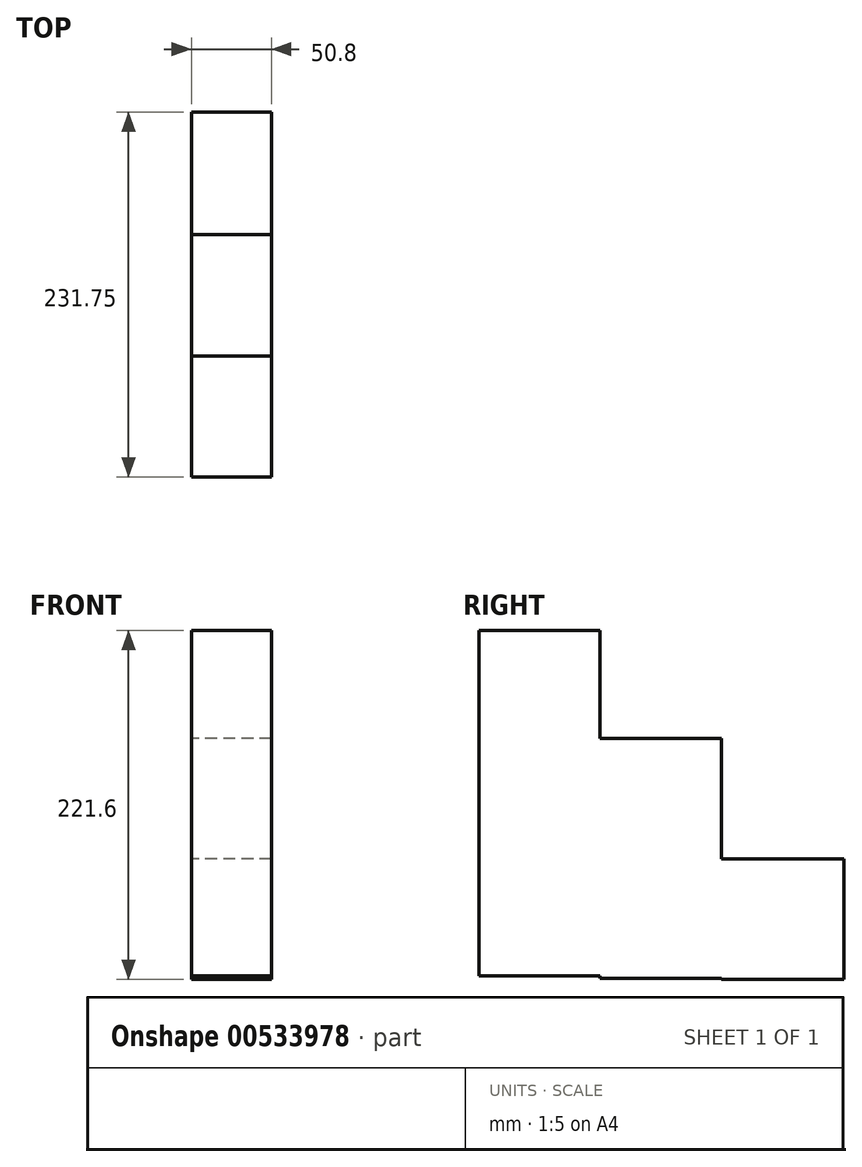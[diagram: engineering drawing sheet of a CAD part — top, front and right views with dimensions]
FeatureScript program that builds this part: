
annotation { "Feature Type Name" : "Feature", "Feature Type Description" : "" }
export const myFeature = defineFeature(function(context is Context, id is Id, definition is map)
    precondition{}
    {
        {
            var Q0;
            Q0=qCreatedBy(makeId("Right.planeOp"),FACE);
            var sketch = newSketch(context, id + "F0", { "sketchPlane" : qUnion([Q0])});
            skLineSegment(sketch, "E0.bottom", {"start": v(0, 0) * mm, "end": v(77.16, 0) * mm});
            skLineSegment(sketch, "E0.top", {"start": v(0, 76.44) * mm, "end": v(77.16, 76.44) * mm});
            skLineSegment(sketch, "E0.left", {"start": v(0, 0) * mm, "end": v(0, 76.44) * mm});
            skLineSegment(sketch, "E0.right", {"start": v(77.16, 0) * mm, "end": v(77.16, 76.44) * mm});
            skLineSegment(sketch, "E1.top", {"start": v(0, -75.96) * mm, "end": v(77.16, -75.96) * mm});
            skLineSegment(sketch, "E1.left", {"start": v(0, 0) * mm, "end": v(0, -75.96) * mm});
            skLineSegment(sketch, "E1.right", {"start": v(77.16, 0) * mm, "end": v(77.16, -75.96) * mm});
            skLineSegment(sketch, "E2.bottom", {"start": v(0, 76.44) * mm, "end": v(-76.7, 76.44) * mm});
            skLineSegment(sketch, "E2.top", {"start": v(0, -74.5) * mm, "end": v(-76.7, -74.5) * mm});
            skLineSegment(sketch, "E2.left", {"start": v(0, 76.44) * mm, "end": v(0, -74.5) * mm});
            skLineSegment(sketch, "E2.right", {"start": v(-76.7, 76.44) * mm, "end": v(-76.7, -74.5) * mm});
            skLineSegment(sketch, "E3.bottom", {"start": v(-76.7, 76.44) * mm, "end": v(0, 76.44) * mm});
            skLineSegment(sketch, "E3.top", {"start": v(-76.7, 135.15) * mm, "end": v(0, 135.15) * mm});
            skLineSegment(sketch, "E3.left", {"start": v(-76.7, 76.44) * mm, "end": v(-76.7, 135.15) * mm});
            skLineSegment(sketch, "E3.right", {"start": v(0, 76.44) * mm, "end": v(0, 135.15) * mm});
            skLineSegment(sketch, "E4.bottom", {"start": v(0, 135.15) * mm, "end": v(-76.7, 135.15) * mm});
            skLineSegment(sketch, "E4.top", {"start": v(0, 144.96) * mm, "end": v(-76.7, 144.96) * mm});
            skLineSegment(sketch, "E4.left", {"start": v(0, 135.15) * mm, "end": v(0, 144.96) * mm});
            skLineSegment(sketch, "E4.right", {"start": v(-76.7, 135.15) * mm, "end": v(-76.7, 144.96) * mm});
            skLineSegment(sketch, "E5.bottom", {"start": v(77.16, 0) * mm, "end": v(155.05, 0) * mm});
            skLineSegment(sketch, "E5.top", {"start": v(77.16, -76.64) * mm, "end": v(155.05, -76.64) * mm});
            skLineSegment(sketch, "E5.left", {"start": v(77.16, 0) * mm, "end": v(77.16, -76.64) * mm});
            skLineSegment(sketch, "E5.right", {"start": v(155.05, 0) * mm, "end": v(155.05, -76.64) * mm});
            skSolve(sketch);
        }
        {
            var Q0;
            Q0 = qSketchRegion(id + "F0", true);
            extrude(context, id + "F1", {"entities" : qUnion([Q0]), "depth" : 25.4 * mm, "offsetDistance" : 25.4 * mm});
        }
        {
            var Q0;
            Q0=makeQuery(id+"F1.opExtrude","CAP_FACE",FACE,{"disambiguationData":[OSD([sQuery(id+"F0.wireOp",EDGE,"E0.top"),sQuery(id+"F0.wireOp",EDGE,"E0.right"),sQuery(id+"F0.wireOp",EDGE,"E1.top"),sQuery(id+"F0.wireOp",EDGE,"E1.left"),sQuery(id+"F0.wireOp",EDGE,"E2.top"),sQuery(id+"F0.wireOp",EDGE,"E2.right"),sQuery(id+"F0.wireOp",EDGE,"E3.left"),sQuery(id+"F0.wireOp",EDGE,"E3.right"),sQuery(id+"F0.wireOp",EDGE,"E4.top"),sQuery(id+"F0.wireOp",EDGE,"E4.left"),sQuery(id+"F0.wireOp",EDGE,"E4.right"),sQuery(id+"F0.wireOp",EDGE,"E5.bottom"),sQuery(id+"F0.wireOp",EDGE,"E5.top"),sQuery(id+"F0.wireOp",EDGE,"E5.left"),sQuery(id+"F0.wireOp",EDGE,"E5.right")])],"isStart":false});
            extrude(context, id + "F2", {"entities" : qUnion([Q0]), "operationType" : NewBodyOperationType.ADD, "oppositeDirection" : true, "depth" : 25.4 * mm, "offsetDistance" : 25.4 * mm});
        }
        {
            var Q0;
            Q0=makeQuery(id+"F1.opExtrude","CAP_FACE",FACE,{"disambiguationData":[OSD([sQuery(id+"F0.wireOp",EDGE,"E0.top"),sQuery(id+"F0.wireOp",EDGE,"E0.right"),sQuery(id+"F0.wireOp",EDGE,"E1.top"),sQuery(id+"F0.wireOp",EDGE,"E1.left"),sQuery(id+"F0.wireOp",EDGE,"E2.top"),sQuery(id+"F0.wireOp",EDGE,"E2.right"),sQuery(id+"F0.wireOp",EDGE,"E3.left"),sQuery(id+"F0.wireOp",EDGE,"E3.right"),sQuery(id+"F0.wireOp",EDGE,"E4.top"),sQuery(id+"F0.wireOp",EDGE,"E4.left"),sQuery(id+"F0.wireOp",EDGE,"E4.right"),sQuery(id+"F0.wireOp",EDGE,"E5.bottom"),sQuery(id+"F0.wireOp",EDGE,"E5.top"),sQuery(id+"F0.wireOp",EDGE,"E5.left"),sQuery(id+"F0.wireOp",EDGE,"E5.right")])],"isStart":false});
            extrude(context, id + "F3", {"entities" : qUnion([Q0]), "operationType" : NewBodyOperationType.ADD, "depth" : 25.4 * mm, "offsetDistance" : 25.4 * mm});
        }
    });
